# Revit family: Hekatron_Raumlufttechnik_LRS 04 Ex_DE_22.01
name_source: partatom
category: Brandmelder
revit_build: Autodesk Revit 2018 (Build: 20190510_1515(x64)
units: mm (PartAtom-declared; Revit-internal decimal feet)

## family parameters
Basisbauteil = Fläche
Beim Laden mit Abzugskörper schneiden = Nein
Bemaßung runder Anschluss = Durchmesser verwenden
Beschriftungsausrichtung beibehalten = Ja
Gemeinsam genutzt = Nein
OmniClass-Nummer = 23.85.30.21
OmniClass-Titel = Environmental Detection/Registration
Raumberechnungspunkt = Nein
Teiletyp = Normal

## types (1)
- LRS 04 Ex
    Ansprechtemperatur = 75.0
    Beschreibung = Lüftungs-Rauchschalter-System zur Rauchüberwachung von Lüftungsleitungen in explosionsgefährdeten Bereichen der Zone 1 und Zone 2.
    Betriebsspannung = 24 V DC
    Breite (mm) = 520.0
    Ex-Zonen = 1, 2, 22
    Farbe = blau
    Funktionsprinzip = optisch
    Hersteller = Hekatron
    Höhe (mm) = 441.0
    Kabeleinführung = oben, unten
    Link zu Ausschreibungstext = https://www.meinhplus.de
    Link zu Produktinformation = https://www.hekatron-planungstools.de
    Link zu ausschreiben.de = http://www.ausschreiben.de
    Material = PC / eloxiertes Alurohr
    Modell = LRS 04 Ex
    Montageart = am Kanal
    Nettogewicht (g) = 2740.0
    Schutzart = IP 54
    Stromaufnahme = max. 12mA
    Tiefe (mm) = 135.0
    Typenkommentare = Lüftungs Rauchschalter System 04 für Ex-gefährdete Bereiche
    UB A&S Artikel Nummer = 31-5000006-01-01
    URL = https://www.hekatron-brandschutz.de
    Version des BIM Objektes = 22.01
    Vorgabe-Ansicht = 1200 mm
    Zulässige Luftgeschwindigkeit = 1 bis 20 m/s
    Zulässige Umgebungstemperatur = -20° C bis +70 °C

## geometry (parser evidence)
native form markers: Sweep x1
no freeform markers — native parametric forms only
